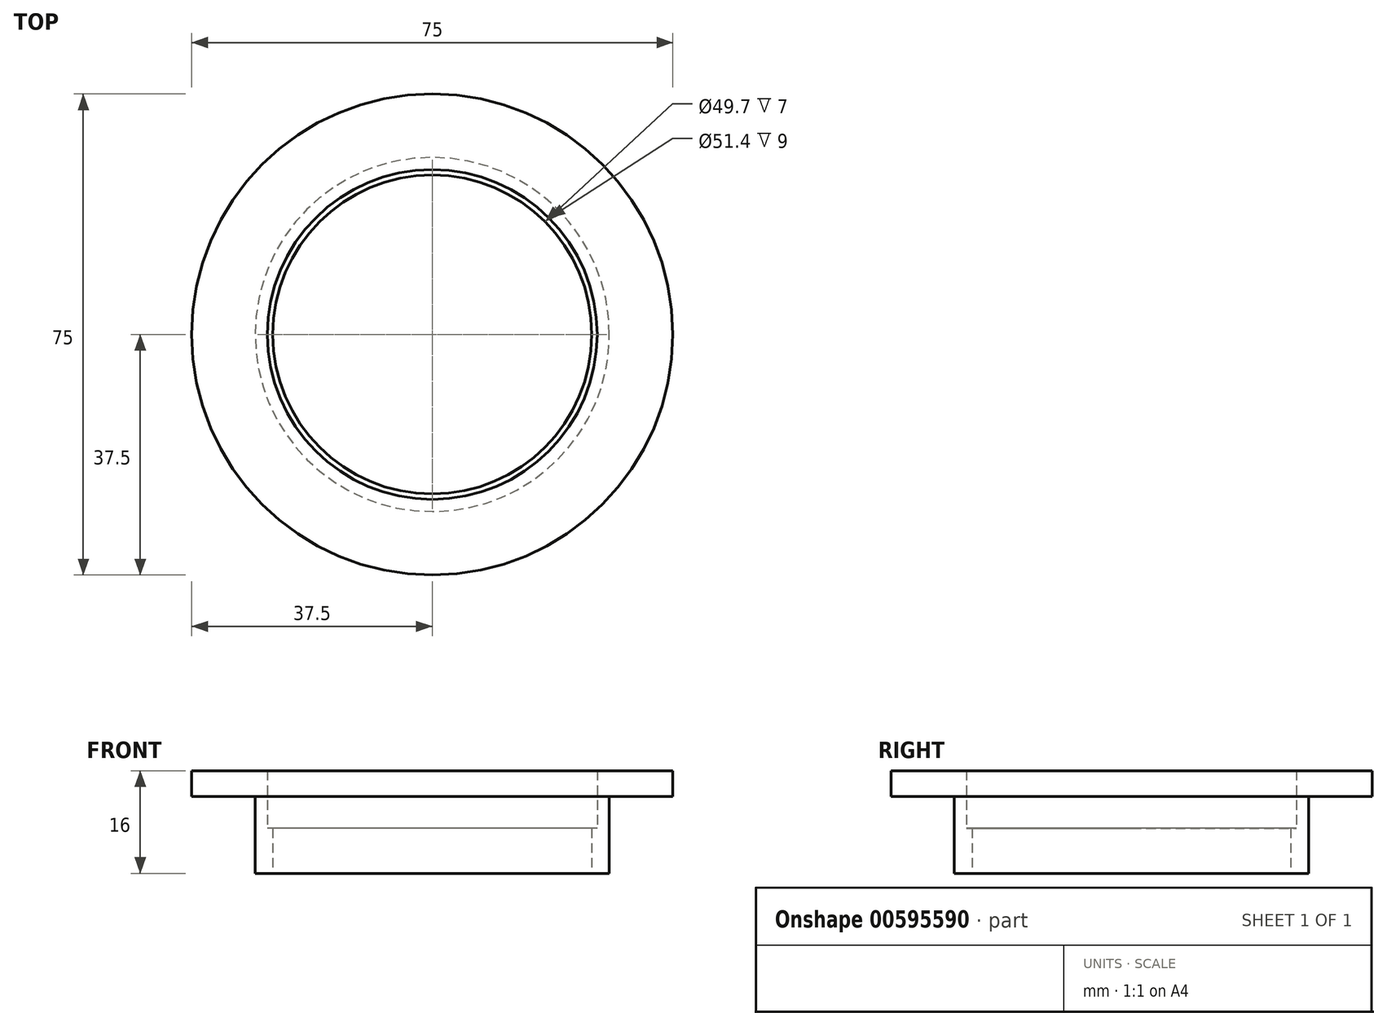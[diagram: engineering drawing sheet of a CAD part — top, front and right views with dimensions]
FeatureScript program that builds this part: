
annotation { "Feature Type Name" : "Feature", "Feature Type Description" : "" }
export const myFeature = defineFeature(function(context is Context, id is Id, definition is map)
    precondition{}
    {
        {
            var Q0;
            Q0=qCreatedBy(makeId("Top.planeOp"),FACE);
            var sketch = newSketch(context, id + "F0", { "sketchPlane" : qUnion([Q0])});
            skCircle(sketch, "E0", {"center": v(0, 0) * mm, "radius": 24.85 * mm});
            skCircle(sketch, "E1", {"center": v(0, 0) * mm, "radius": 25.7 * mm});
            skSolve(sketch);
        }
        {
            var Q0;
            Q0 = qSketchRegion(id + "F0", true);
            extrude(context, id + "F1", {"entities" : qUnion([Q0]), "depth" : 7 * mm, "offsetDistance" : 25 * mm});
        }
        {
            var Q0;
            Q0=qCreatedBy(makeId("Top.planeOp"),FACE);
            var sketch = newSketch(context, id + "F2", { "sketchPlane" : qUnion([Q0])});
            skCircle(sketch, "E2", {"center": v(0, 0) * mm, "radius": 25.7 * mm});
            skCircle(sketch, "E3", {"center": v(0, 0) * mm, "radius": 27.6 * mm});
            skSolve(sketch);
        }
        {
            var Q0;
            Q0 = qSketchRegion(id + "F2", true);
            extrude(context, id + "F3", {"entities" : qUnion([Q0]), "operationType" : NewBodyOperationType.ADD, "depth" : 12 * mm, "offsetDistance" : 25 * mm});
        }
        {
            var Q0;
            Q0=qCreatedBy(makeId("Top.planeOp"),FACE);
            cPlane(context, id + "F4", {"entities" : qUnion([Q0]), "cplaneType" : CPlaneType.OFFSET, "offset" : 12 * mm, "width" : 150 * mm, "height" : 150 * mm});
        }
        {
            var Q0;
            Q0=qCreatedBy(id+"F4.planeOp",FACE);
            var sketch = newSketch(context, id + "F5", { "sketchPlane" : qUnion([Q0])});
            skCircle(sketch, "E4", {"center": v(0, 0) * mm, "radius": 37.5 * mm});
            skCircle(sketch, "E5", {"center": v(0, 0) * mm, "radius": 25.7 * mm});
            skSolve(sketch);
        }
        {
            var Q0;
            Q0 = qSketchRegion(id + "F5", true);
            extrude(context, id + "F6", {"entities" : qUnion([Q0]), "operationType" : NewBodyOperationType.ADD, "depth" : 4 * mm, "offsetDistance" : 25 * mm});
        }
    });
